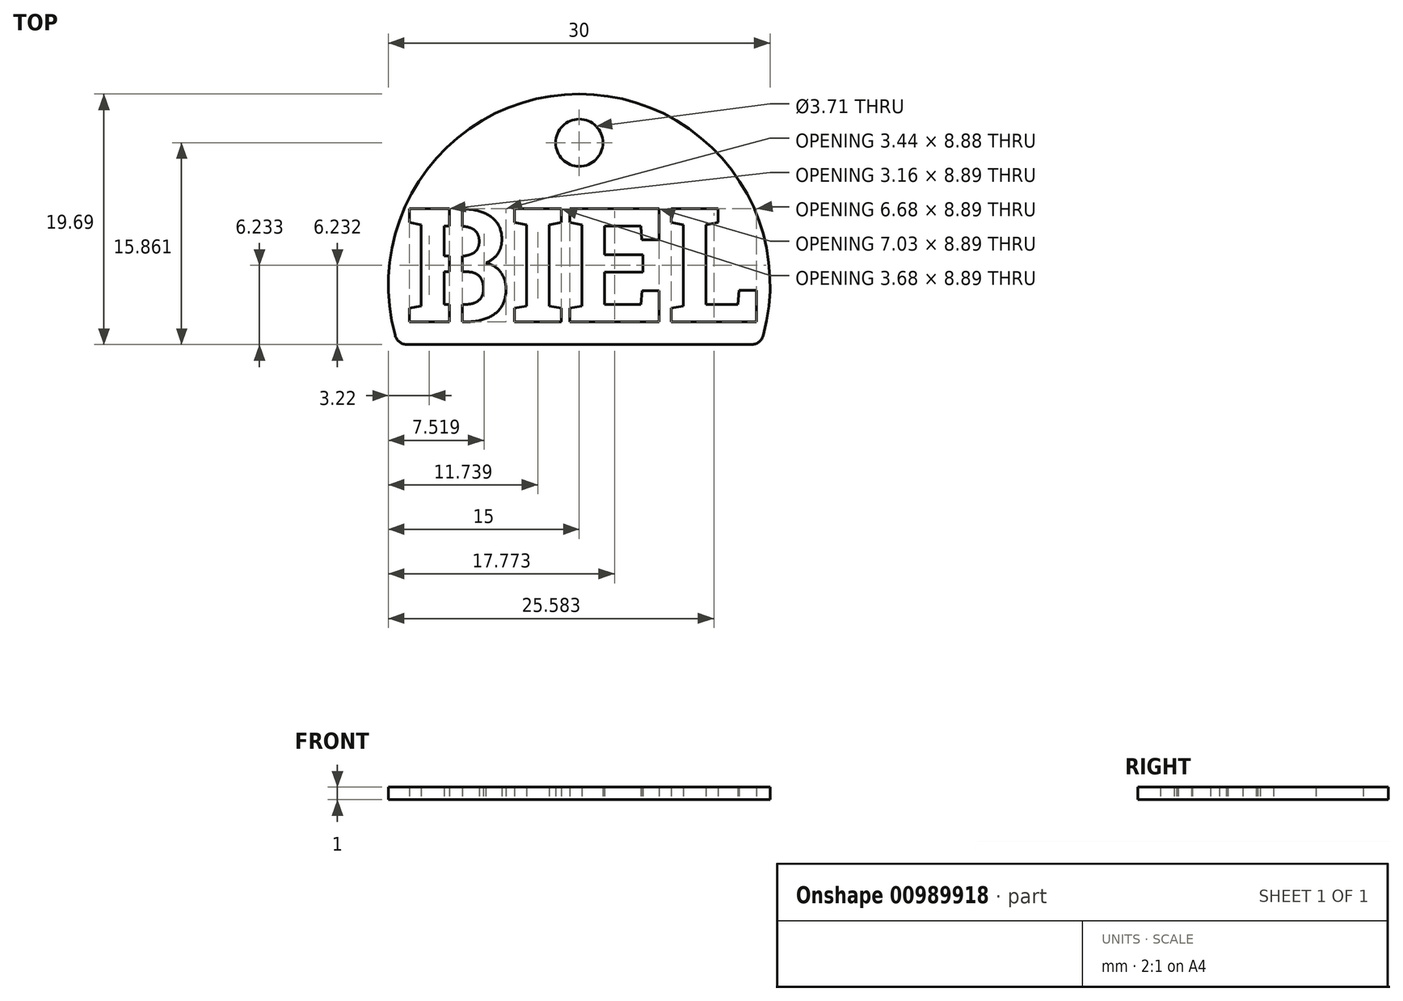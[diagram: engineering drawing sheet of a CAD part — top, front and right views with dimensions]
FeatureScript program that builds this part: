
annotation { "Feature Type Name" : "Feature", "Feature Type Description" : "" }
export const myFeature = defineFeature(function(context is Context, id is Id, definition is map)
    precondition{}
    {
        {
            var Q0;
            Q0=qCreatedBy(makeId("Top.planeOp"),FACE);
            var sketch = newSketch(context, id + "F0", { "sketchPlane" : qUnion([Q0])});
            skArc(sketch, "E0", {"start": v(14.47, -3.95) * mm, "mid": v(0, 15) * mm, "end": v(-14.47, -3.95) * mm});
            skText(sketch, "E1", { "text": "BIEL", "fontName": "RobotoSlab-Bold.ttf"});
            skLineSegment(sketch, "E2.bottom", {"start": v(-9.6, 6.1) * mm, "end": v(-9.06, 6.1) * mm});
            skLineSegment(sketch, "E2.top", {"start": v(-9.6, -2.9) * mm, "end": v(-9.06, -2.9) * mm});
            skLineSegment(sketch, "E3.bottom", {"start": v(-10.2, 6.1) * mm, "end": v(-9.2, 6.1) * mm});
            skLineSegment(sketch, "E3.top", {"start": v(-10.2, -2.9) * mm, "end": v(-9.2, -2.9) * mm});
            skLineSegment(sketch, "E3.left", {"start": v(-10.2, 6.1) * mm, "end": v(-10.2, -2.9) * mm});
            skLineSegment(sketch, "E3.right", {"start": v(-9.2, 6.1) * mm, "end": v(-9.2, -2.9) * mm});
            skCircle(sketch, "E4", {"center": v(0, 11.17) * mm, "radius": 1.85 * mm});
            skLineSegment(sketch, "E5", {"start": v(-13.5, -4.69) * mm, "end": v(13.5, -4.69) * mm});
            skPoint(sketch, "E6.visualSharp", {"position": v(-14.25, -4.69) * mm});
            skArc(sketch, "E6.filletArc", {"start": v(-14.47, -3.95) * mm, "mid": v(-14.11, -4.48) * mm, "end": v(-13.5, -4.69) * mm});
            skPoint(sketch, "E7.visualSharp", {"position": v(14.25, -4.69) * mm});
            skArc(sketch, "E7.filletArc", {"start": v(13.5, -4.69) * mm, "mid": v(14.11, -4.48) * mm, "end": v(14.47, -3.95) * mm});
            const initialGuessF0  = {"E1": [-0.0137, -0.0029, 1, 0, 0.009]};
            skSetInitialGuess(sketch, initialGuessF0);
            skSolve(sketch);
        }
        {
            var Q0;
            Q0 = qSketchRegion(id + "F0", true);
            extrude(context, id + "F1", {"entities" : qUnion([Q0]), "depth" : 1 * mm, "offsetDistance" : 25.4 * mm});
        }
        {
            var Q0;
            {var subQ0=sQuery(id+"F0.wireOp",EDGE,"E1.sketch_text.stroke-29");Q0=makeQuery(id+"F0.imprint","IMPRINT",FACE,{"disambiguationData":[TD([[makeQuery(id+"F0.imprint","IMPRINT",EDGE,{"derivedFrom":subQ0}),1.0]])]});}
            var Q1;
            {var subQ7=sQuery(id+"F0.wireOp",EDGE,"E1.sketch_text.stroke-24");var subQ9=sQuery(id+"F0.wireOp",EDGE,"E1.sketch_text.stroke-23");var subQ10=makeQuery(id+"F0.imprint","INTERSECT",VERTEX,{"derivedFrom":[subQ9,subQ7]});Q1=makeQuery(id+"F0.imprint","IMPRINT",FACE,{"disambiguationData":[TD([[makeQuery(id+"F0.imprint","IMPRINT",EDGE,{"disambiguationData":[TD([[subQ10,1.0]])],"derivedFrom":subQ9}),1.0]])]});}
            var Q2;
            {var subQ4=sQuery(id+"F0.wireOp",EDGE,"E1.sketch_text.stroke-25");Q2=makeQuery(id+"F0.imprint","IMPRINT",FACE,{"disambiguationData":[TD([[makeQuery(id+"F0.imprint","IMPRINT",EDGE,{"derivedFrom":subQ4}),1.0]])]});}
            var Q3;
            {var subQ0=sQuery(id+"F0.wireOp",EDGE,"E1.sketch_text.stroke-18");Q3=makeQuery(id+"F0.imprint","IMPRINT",FACE,{"disambiguationData":[TD([[makeQuery(id+"F0.imprint","IMPRINT",EDGE,{"derivedFrom":subQ0}),1.0]])]});}
            var Q4;
            {var subQ0=sQuery(id+"F0.wireOp",EDGE,"E3.left");var subQ1=sQuery(id+"F0.wireOp",EDGE,"E1.sketch_text.stroke-17");var subQ2=makeQuery(id+"F0.imprint","INTERSECT",VERTEX,{"derivedFrom":[subQ1,subQ0]});Q4=makeQuery(id+"F0.imprint","IMPRINT",FACE,{"disambiguationData":[TD([[makeQuery(id+"F0.imprint","IMPRINT",EDGE,{"disambiguationData":[TD([[subQ2,-1.0]])],"derivedFrom":subQ1}),1.0]])]});}
            var Q5;
            {var subQ0=sQuery(id+"F0.wireOp",EDGE,"E1.sketch_text.stroke-16");Q5=makeQuery(id+"F0.imprint","IMPRINT",FACE,{"disambiguationData":[TD([[makeQuery(id+"F0.imprint","IMPRINT",EDGE,{"derivedFrom":subQ0}),1.0]])]});}
            var Q6;
            {var subQ3=sQuery(id+"F0.wireOp",EDGE,"E3.right");var subQ6=sQuery(id+"F0.wireOp",EDGE,"E1.sketch_text.stroke-22");var subQ9=makeQuery(id+"F0.imprint","INTERSECT",VERTEX,{"derivedFrom":[subQ6,subQ3]});Q6=makeQuery(id+"F0.imprint","IMPRINT",FACE,{"disambiguationData":[TD([[makeQuery(id+"F0.imprint","IMPRINT",EDGE,{"disambiguationData":[TD([[subQ9,-1.0]])],"derivedFrom":subQ6}),-1.0]])]});}
            var Q7;
            {var subQ0=sQuery(id+"F0.wireOp",EDGE,"E3.left");var subQ3=sQuery(id+"F0.wireOp",EDGE,"E1.sketch_text.stroke-17");var subQ4=makeQuery(id+"F0.imprint","INTERSECT",VERTEX,{"derivedFrom":[subQ3,subQ0]});Q7=makeQuery(id+"F0.imprint","IMPRINT",FACE,{"disambiguationData":[TD([[makeQuery(id+"F0.imprint","IMPRINT",EDGE,{"disambiguationData":[TD([[subQ4,-1.0]])],"derivedFrom":subQ3}),-1.0]])]});}
            var Q8;
            {var subQ7=sQuery(id+"F0.wireOp",EDGE,"E1.sketch_text.stroke-15");var subQ8=sQuery(id+"F0.wireOp",EDGE,"E1.sketch_text.stroke-0");var subQ9=makeQuery(id+"F0.imprint","INTERSECT",VERTEX,{"derivedFrom":[subQ8,subQ7]});Q8=makeQuery(id+"F0.imprint","IMPRINT",FACE,{"disambiguationData":[TD([[makeQuery(id+"F0.imprint","IMPRINT",EDGE,{"disambiguationData":[TD([[subQ9,-1.0]])],"derivedFrom":subQ8}),-1.0]])]});}
            var Q9;
            {var subQ1=sQuery(id+"F0.wireOp",EDGE,"E3.bottom");var subQ3=makeQuery(id+"F0.imprint","IMPRINT",VERTEX,{"derivedFrom":subQ1});Q9=makeQuery(id+"F0.imprint","IMPRINT",FACE,{"disambiguationData":[TD([[makeQuery(id+"F0.imprint","IMPRINT",EDGE,{"disambiguationData":[TD([[subQ3,1.0]])],"derivedFrom":subQ1}),-1.0]])]});}
            extrude(context, id + "F2", {"entities" : qUnion([Q0, Q1, Q2, Q3, Q4, Q5, Q6, Q7, Q8, Q9]), "operationType" : NewBodyOperationType.ADD, "depth" : 1 * mm, "offsetDistance" : 25.4 * mm});
        }
    });
